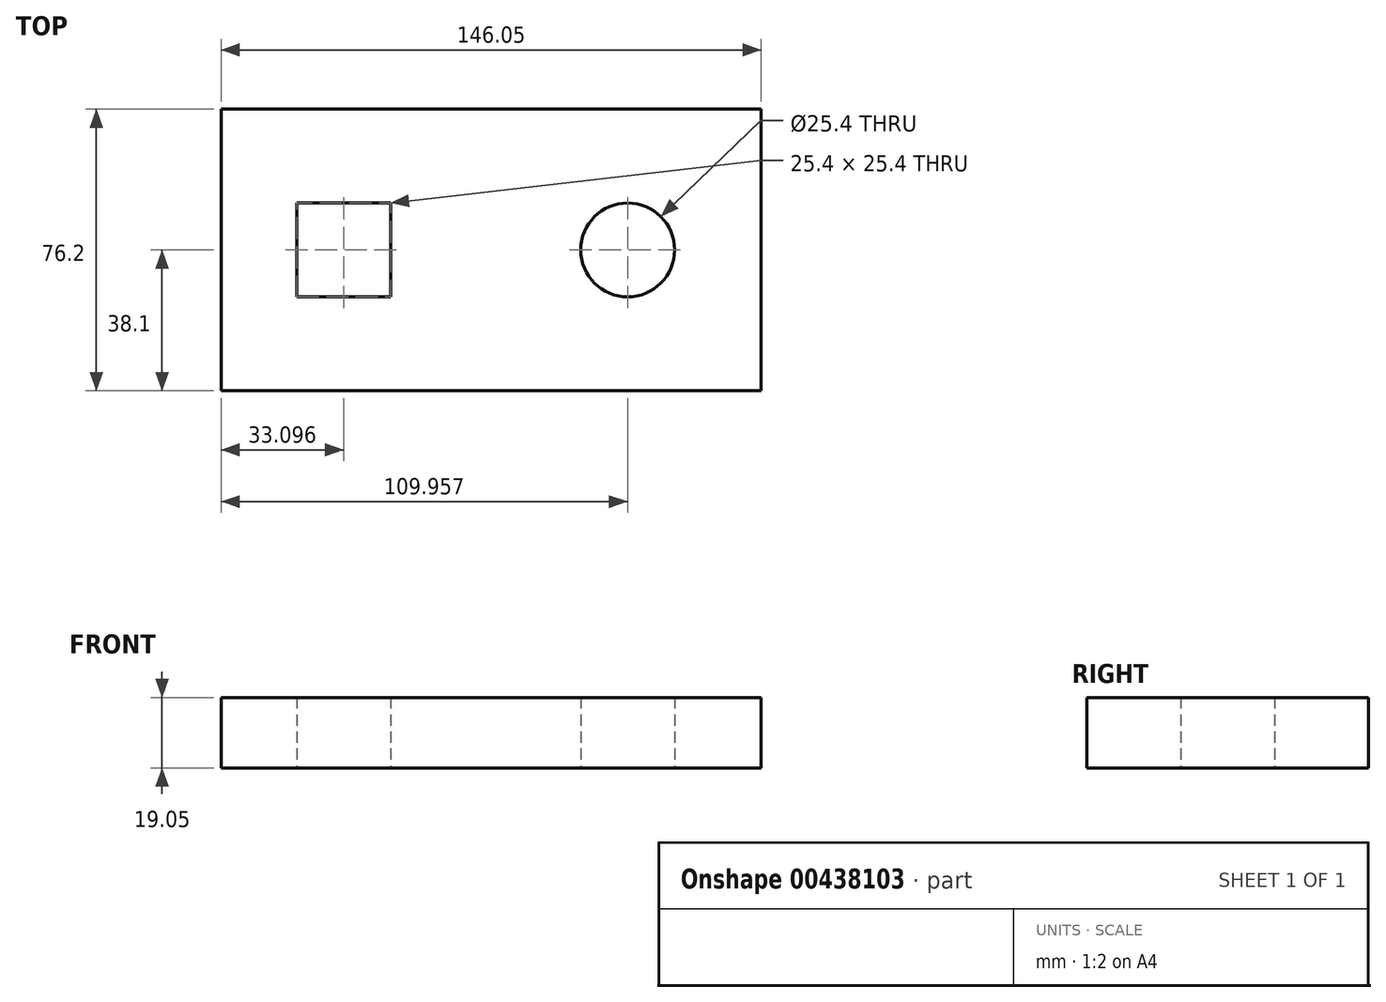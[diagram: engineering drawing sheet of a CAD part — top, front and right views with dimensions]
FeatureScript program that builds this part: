
annotation { "Feature Type Name" : "Feature", "Feature Type Description" : "" }
export const myFeature = defineFeature(function(context is Context, id is Id, definition is map)
    precondition{}
    {
        {
            var Q0;
            Q0=qCreatedBy(makeId("Top.planeOp"),FACE);
            var sketch = newSketch(context, id + "F0", { "sketchPlane" : qUnion([Q0])});
            skLineSegment(sketch, "E0.bottom", {"start": v(-71.97, 38.1) * mm, "end": v(74.08, 38.1) * mm});
            skLineSegment(sketch, "E0.top", {"start": v(-71.97, -38.1) * mm, "end": v(74.08, -38.1) * mm});
            skLineSegment(sketch, "E0.left", {"start": v(-71.97, 38.1) * mm, "end": v(-71.97, -38.1) * mm});
            skLineSegment(sketch, "E0.right", {"start": v(74.08, 38.1) * mm, "end": v(74.08, -38.1) * mm});
            skLineSegment(sketch, "E1.bottom", {"start": v(-51.57, 12.7) * mm, "end": v(-26.17, 12.7) * mm});
            skLineSegment(sketch, "E1.top", {"start": v(-51.57, -12.7) * mm, "end": v(-26.17, -12.7) * mm});
            skLineSegment(sketch, "E1.left", {"start": v(-51.57, 12.7) * mm, "end": v(-51.57, -12.7) * mm});
            skLineSegment(sketch, "E1.right", {"start": v(-26.17, 12.7) * mm, "end": v(-26.17, -12.7) * mm});
            skCircle(sketch, "E2", {"center": v(37.99, 0) * mm, "radius": 12.7 * mm});
            skSolve(sketch);
        }
        {
            var Q0;
            Q0=makeQuery(id+"F0.imprint","IMPRINT",FACE,{"disambiguationData":[TD([[makeQuery(id+"F0.imprint","IMPRINT",EDGE,{"derivedFrom":sQuery(id+"F0.wireOp",EDGE,"E0.bottom")}),-1.0]])]});
            extrude(context, id + "F1", {"entities" : qUnion([Q0]), "depth" : 19.05 * mm});
        }
    });
